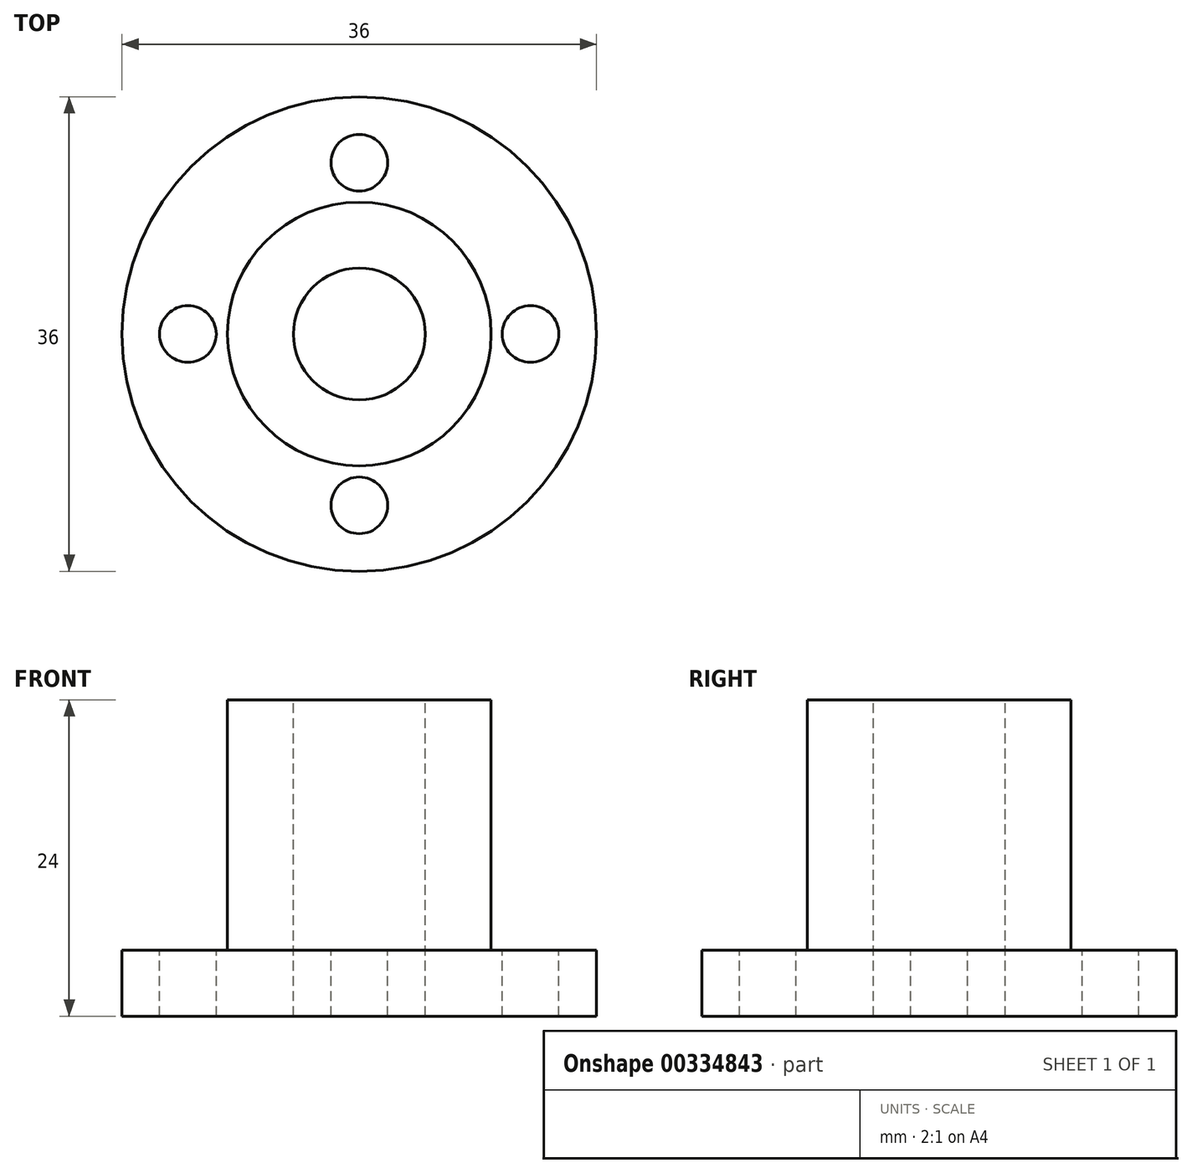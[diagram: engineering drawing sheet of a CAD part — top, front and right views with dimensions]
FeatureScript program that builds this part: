
annotation { "Feature Type Name" : "Feature", "Feature Type Description" : "" }
export const myFeature = defineFeature(function(context is Context, id is Id, definition is map)
    precondition{}
    {
        {
            var Q0;
            Q0=qCreatedBy(makeId("Top.planeOp"),FACE);
            var sketch = newSketch(context, id + "F0", { "sketchPlane" : qUnion([Q0])});
            skCircle(sketch, "E0", {"center": v(0, 0) * mm, "radius": 18 * mm});
            skSolve(sketch);
        }
        {
            var Q0;
            Q0 = qSketchRegion(id + "F0", true);
            extrude(context, id + "F1", {"entities" : qUnion([Q0]), "depth" : 5 * mm});
        }
        {
            var Q0;
            Q0=makeQuery(id+"F1.opExtrude","CAP_FACE",FACE,{"disambiguationData":[OSD([sQuery(id+"F0.wireOp",EDGE,"E0")])],"isStart":false});
            var sketch = newSketch(context, id + "F2", { "sketchPlane" : qUnion([Q0])});
            skCircle(sketch, "E1", {"center": v(0, 0) * mm, "radius": 10 * mm});
            skSolve(sketch);
        }
        {
            var Q0;
            Q0 = qSketchRegion(id + "F2", true);
            extrude(context, id + "F3", {"entities" : qUnion([Q0]), "operationType" : NewBodyOperationType.ADD, "depth" : (24 - 5) * mm});
        }
        {
            var Q0;
            Q0=makeQuery(id+"F3.opExtrude","CAP_FACE",FACE,{"disambiguationData":[OSD([sQuery(id+"F2.wireOp",EDGE,"E1")])],"isStart":false});
            var sketch = newSketch(context, id + "F4", { "sketchPlane" : qUnion([Q0])});
            skCircle(sketch, "E2", {"center": v(0, 0) * mm, "radius": 5 * mm});
            skSolve(sketch);
        }
        {
            var Q0;
            Q0 = qSketchRegion(id + "F4", true);
            extrude(context, id + "F5", {"entities" : qUnion([Q0]), "operationType" : NewBodyOperationType.REMOVE, "oppositeDirection" : true, "depth" : 25 * mm});
        }
        {
            var Q0;
            Q0=makeQuery(id+"F1.opExtrude","CAP_FACE",FACE,{"disambiguationData":[OSD([sQuery(id+"F0.wireOp",EDGE,"E0")])],"isStart":false});
            var sketch = newSketch(context, id + "F6", { "sketchPlane" : qUnion([Q0])});
            skCircle(sketch, "E3", {"center": v(0, 13) * mm, "radius": 2.15 * mm});
            skCircle(sketch, "E4.1.0", {"center": v(-13, 0) * mm, "radius": 2.15 * mm});
            skCircle(sketch, "E4.2.0", {"center": v(0, -13) * mm, "radius": 2.15 * mm});
            skCircle(sketch, "E4.3.0", {"center": v(13, 0) * mm, "radius": 2.15 * mm});
            skPoint(sketch, "E4.center", {"position": v(0, 0) * mm});
            skSolve(sketch);
        }
        {
            var Q0;
            Q0 = qSketchRegion(id + "F6", true);
            extrude(context, id + "F7", {"entities" : qUnion([Q0]), "operationType" : NewBodyOperationType.REMOVE, "oppositeDirection" : true, "depth" : 25 * mm});
        }
    });
